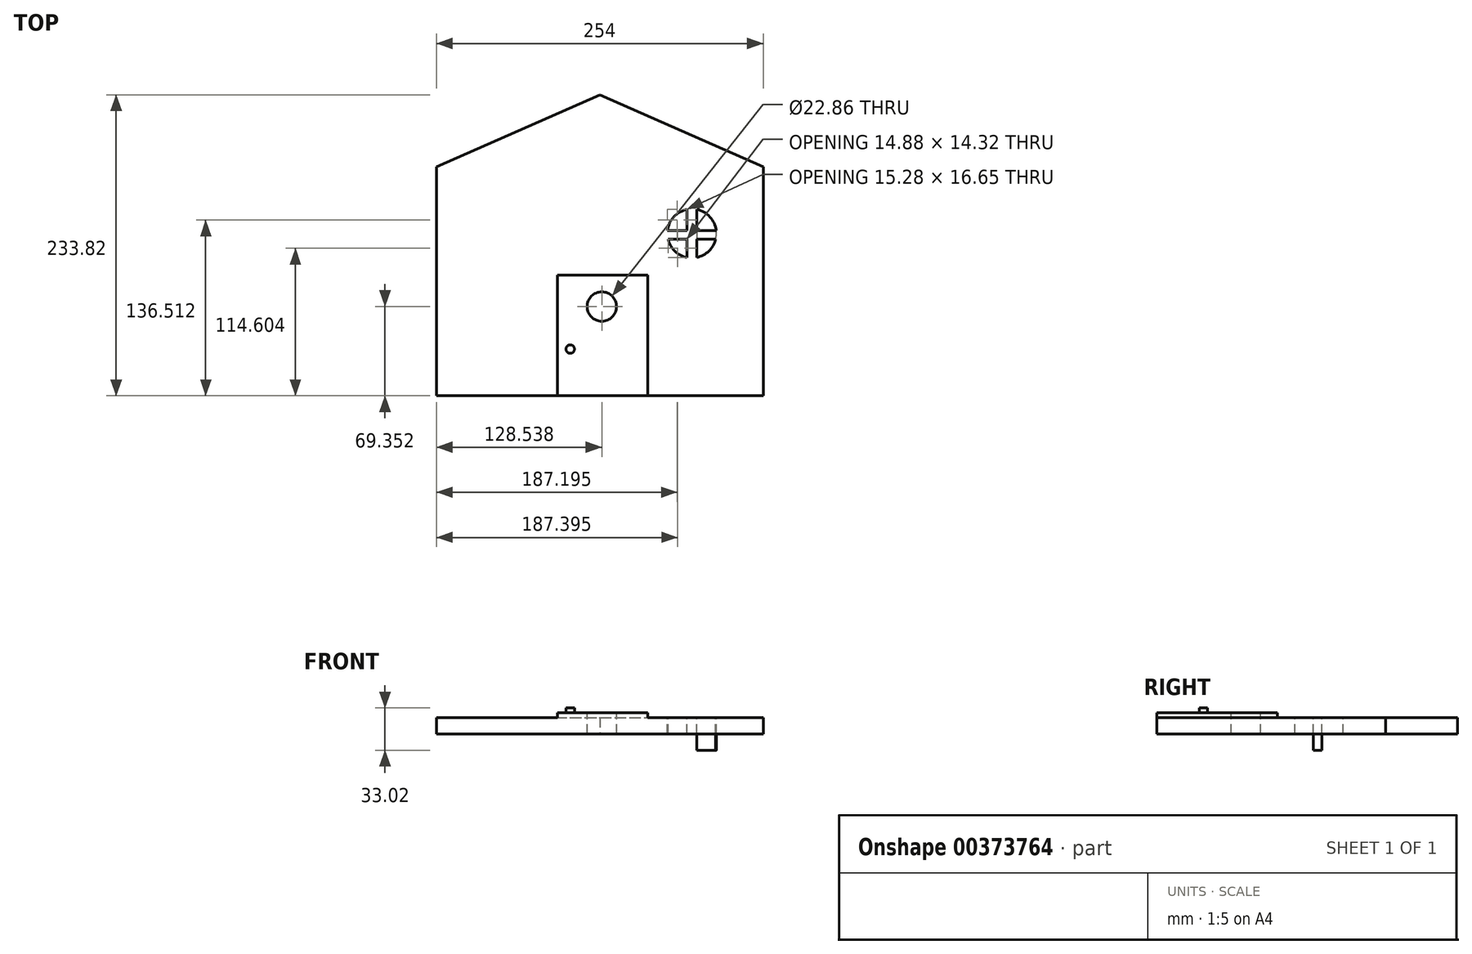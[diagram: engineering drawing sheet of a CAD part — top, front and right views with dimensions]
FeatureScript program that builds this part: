
annotation { "Feature Type Name" : "Feature", "Feature Type Description" : "" }
export const myFeature = defineFeature(function(context is Context, id is Id, definition is map)
    precondition{}
    {
        {
            var Q0;
            Q0=qCreatedBy(makeId("Top.planeOp"),FACE);
            var sketch = newSketch(context, id + "F0", { "sketchPlane" : qUnion([Q0])});
            skLineSegment(sketch, "E0.bottom", {"start": v(-400.1, 213.34) * mm, "end": v(-146.1, 213.34) * mm});
            skLineSegment(sketch, "E0.top", {"start": v(-400.1, 35.54) * mm, "end": v(-146.1, 35.54) * mm});
            skLineSegment(sketch, "E0.left", {"start": v(-400.1, 213.34) * mm, "end": v(-400.1, 35.54) * mm});
            skLineSegment(sketch, "E0.right", {"start": v(-146.1, 213.34) * mm, "end": v(-146.1, 35.54) * mm});
            skLineSegment(sketch, "E1", {"start": v(-400.1, 213.34) * mm, "end": v(-273.1, 269.36) * mm});
            skLineSegment(sketch, "E2", {"start": v(-273.1, 269.36) * mm, "end": v(-146.1, 213.34) * mm});
            skPoint(sketch, "E3", {"position": v(-273.1, 213.34) * mm});
            skSolve(sketch);
        }
        {
            var Q0;
            Q0=makeQuery(id+"F0.imprint","IMPRINT",FACE,{"disambiguationData":[TD([[makeQuery(id+"F0.imprint","IMPRINT",EDGE,{"derivedFrom":sQuery(id+"F0.wireOp",EDGE,"E0.bottom")}),-1.0]])]});
            var Q1;
            Q1=makeQuery(id+"F0.imprint","IMPRINT",FACE,{"disambiguationData":[TD([[makeQuery(id+"F0.imprint","IMPRINT",EDGE,{"derivedFrom":sQuery(id+"F0.wireOp",EDGE,"E0.bottom")}),1.0]])]});
            extrude(context, id + "F1", {"entities" : qUnion([Q0, Q1]), "depth" : 12.7 * mm});
        }
        {
            var Q0;
            Q0=makeQuery(id+"F1.opExtrude","CAP_FACE",FACE,{"disambiguationData":[OSD([sQuery(id+"F0.wireOp",EDGE,"E0.top"),sQuery(id+"F0.wireOp",EDGE,"E0.left"),sQuery(id+"F0.wireOp",EDGE,"E0.right"),sQuery(id+"F0.wireOp",EDGE,"E1"),sQuery(id+"F0.wireOp",EDGE,"E2")])],"isStart":false});
            var sketch = newSketch(context, id + "F2", { "sketchPlane" : qUnion([Q0])});
            skCircle(sketch, "E4", {"center": v(-201.6, 161.68) * mm, "radius": 18.7 * mm});
            skSolve(sketch);
        }
        {
            var Q0;
            Q0=sQuery(id+"F2.wireOp",VERTEX,"E4.center");
            var Q1;
            Q1=makeQuery(id+"F1.opExtrude","SWEPT_BODY",BODY,{"disambiguationData":[OSD([sQuery(id+"F0.wireOp",EDGE,"E0.top"),sQuery(id+"F0.wireOp",EDGE,"E0.left"),sQuery(id+"F0.wireOp",EDGE,"E0.right"),sQuery(id+"F0.wireOp",EDGE,"E1"),sQuery(id+"F0.wireOp",EDGE,"E2")])]});
            hole(context, id + "F3", {"style" : HoleStyle.SIMPLE, "endStyle" : HoleEndStyle.THROUGH, "holeDiameter" : 38.1 * mm, "isTappedThrough" : true, "tappedDepth" : 12.7 * mm, "tapClearance" : 3, "locations" : qUnion([Q0]), "scope" : qUnion([Q1])});
        }
        {
            var Q0;
            Q0=makeQuery(id+"F1.opExtrude","CAP_FACE",FACE,{"disambiguationData":[OSD([sQuery(id+"F0.wireOp",EDGE,"E0.top"),sQuery(id+"F0.wireOp",EDGE,"E0.left"),sQuery(id+"F0.wireOp",EDGE,"E0.right"),sQuery(id+"F0.wireOp",EDGE,"E1"),sQuery(id+"F0.wireOp",EDGE,"E2")])],"isStart":false});
            var sketch = newSketch(context, id + "F4", { "sketchPlane" : qUnion([Q0])});
            skLineSegment(sketch, "E5.bottom", {"start": v(-306.13, 35.54) * mm, "end": v(-236, 35.54) * mm});
            skLineSegment(sketch, "E5.top", {"start": v(-306.13, 129.3) * mm, "end": v(-236, 129.3) * mm});
            skLineSegment(sketch, "E5.left", {"start": v(-306.13, 35.54) * mm, "end": v(-306.13, 129.3) * mm});
            skLineSegment(sketch, "E5.right", {"start": v(-236, 35.54) * mm, "end": v(-236, 129.3) * mm});
            skSolve(sketch);
        }
        {
            var Q0;
            Q0=makeQuery(id+"F4.imprint","IMPRINT",FACE,{"disambiguationData":[TD([[makeQuery(id+"F4.imprint","IMPRINT",EDGE,{"derivedFrom":sQuery(id+"F4.wireOp",EDGE,"E5.bottom")}),1.0]])]});
            extrude(context, id + "F5", {"entities" : qUnion([Q0]), "operationType" : NewBodyOperationType.ADD, "depth" : 3.8 * mm});
        }
        {
            var Q0;
            Q0=makeQuery(id+"F5.opExtrude","CAP_FACE",FACE,{"disambiguationData":[OSD([sQuery(id+"F4.wireOp",EDGE,"E5.bottom"),sQuery(id+"F4.wireOp",EDGE,"E5.top"),sQuery(id+"F4.wireOp",EDGE,"E5.left"),sQuery(id+"F4.wireOp",EDGE,"E5.right")])],"isStart":false});
            var sketch = newSketch(context, id + "F6", { "sketchPlane" : qUnion([Q0])});
            skPoint(sketch, "E6", {"position": v(-271.56, 104.9) * mm});
            skSolve(sketch);
        }
        {
            var Q0;
            Q0=sQuery(id+"F6.wireOp",VERTEX,"E6");
            var Q1;
            Q1=makeQuery(id+"F1.opExtrude","SWEPT_BODY",BODY,{"disambiguationData":[OSD([sQuery(id+"F0.wireOp",EDGE,"E0.top"),sQuery(id+"F0.wireOp",EDGE,"E0.left"),sQuery(id+"F0.wireOp",EDGE,"E0.right"),sQuery(id+"F0.wireOp",EDGE,"E1"),sQuery(id+"F0.wireOp",EDGE,"E2")])]});
            hole(context, id + "F7", {"style" : HoleStyle.SIMPLE, "endStyle" : HoleEndStyle.THROUGH, "holeDiameter" : 22.86 * mm, "isTappedThrough" : true, "tappedDepth" : 12.7 * mm, "tapClearance" : 3, "locations" : qUnion([Q0]), "scope" : qUnion([Q1])});
        }
        {
            var Q0;
            Q0=makeQuery(id+"F1.opExtrude","CAP_FACE",FACE,{"disambiguationData":[OSD([sQuery(id+"F0.wireOp",EDGE,"E0.top"),sQuery(id+"F0.wireOp",EDGE,"E0.left"),sQuery(id+"F0.wireOp",EDGE,"E0.right"),sQuery(id+"F0.wireOp",EDGE,"E1"),sQuery(id+"F0.wireOp",EDGE,"E2")])],"isStart":false});
            var sketch = newSketch(context, id + "F8", { "sketchPlane" : qUnion([Q0])});
            skLineSegment(sketch, "E7", {"start": v(-205.26, 180.37) * mm, "end": v(-205.26, 142.98) * mm});
            skLineSegment(sketch, "E8", {"start": v(-197.77, 180.34) * mm, "end": v(-197.77, 143.02) * mm});
            skLineSegment(sketch, "E9", {"start": v(-220.55, 163.73) * mm, "end": v(-182.67, 163.73) * mm});
            skLineSegment(sketch, "E10", {"start": v(-183.07, 157.3) * mm, "end": v(-220.15, 157.3) * mm});
            skSolve(sketch);
        }
        {
            var Q0;
            {var subQ0=sQuery(id+"F8.wireOp",EDGE,"E7");var subQ3=sQuery(id+"F8.wireOp",EDGE,"E9");var subQ4=makeQuery(id+"F8.imprint","INTERSECT",VERTEX,{"derivedFrom":[subQ0,subQ3]});Q0=makeQuery(id+"F8.imprint","IMPRINT",FACE,{"disambiguationData":[TD([[makeQuery(id+"F8.imprint","IMPRINT",EDGE,{"disambiguationData":[TD([[subQ4,-1.0]])],"derivedFrom":subQ3}),1.0]])]});}
            extrude(context, id + "F9", {"entities" : qUnion([Q0]), "oppositeDirection" : true, "depth" : 12.7 * mm});
        }
        {
            var Q0;
            {var subQ0=sQuery(id+"F8.wireOp",EDGE,"E9");var subQ1=sQuery(id+"F8.wireOp",EDGE,"E7");var subQ2=makeQuery(id+"F8.imprint","INTERSECT",VERTEX,{"derivedFrom":[subQ1,subQ0]});Q0=makeQuery(id+"F8.imprint","IMPRINT",FACE,{"disambiguationData":[TD([[makeQuery(id+"F8.imprint","IMPRINT",EDGE,{"disambiguationData":[TD([[subQ2,-1.0]])],"derivedFrom":subQ1}),1.0]])]});}
            extrude(context, id + "F10", {"entities" : qUnion([Q0]), "operationType" : NewBodyOperationType.ADD, "oppositeDirection" : true, "depth" : 12.7 * mm});
        }
        {
            var Q0;
            {var subQ0=sQuery(id+"F8.wireOp",EDGE,"E7");var subQ3=sQuery(id+"F8.wireOp",EDGE,"E10");var subQ4=makeQuery(id+"F8.imprint","INTERSECT",VERTEX,{"derivedFrom":[subQ0,subQ3]});Q0=makeQuery(id+"F8.imprint","IMPRINT",FACE,{"disambiguationData":[TD([[makeQuery(id+"F8.imprint","IMPRINT",EDGE,{"disambiguationData":[TD([[subQ4,1.0]])],"derivedFrom":subQ3}),1.0]])]});}
            extrude(context, id + "F11", {"entities" : qUnion([Q0]), "operationType" : NewBodyOperationType.ADD, "oppositeDirection" : true, "depth" : 12.7 * mm});
        }
        {
            var Q0;
            {var subQ0=sQuery(id+"F8.wireOp",EDGE,"E9");var subQ1=sQuery(id+"F8.wireOp",EDGE,"E8");var subQ2=makeQuery(id+"F8.imprint","INTERSECT",VERTEX,{"derivedFrom":[subQ1,subQ0]});Q0=makeQuery(id+"F8.imprint","IMPRINT",FACE,{"disambiguationData":[TD([[makeQuery(id+"F8.imprint","IMPRINT",EDGE,{"disambiguationData":[TD([[subQ2,-1.0]])],"derivedFrom":subQ1}),1.0]])]});}
            extrude(context, id + "F12", {"entities" : qUnion([Q0]), "operationType" : NewBodyOperationType.ADD, "oppositeDirection" : true, "depth" : 25.4 * mm});
        }
        {
            var Q0;
            {var subQ0=sQuery(id+"F8.wireOp",EDGE,"E9");var subQ1=sQuery(id+"F8.wireOp",EDGE,"E7");var subQ2=makeQuery(id+"F8.imprint","INTERSECT",VERTEX,{"derivedFrom":[subQ1,subQ0]});Q0=makeQuery(id+"F8.imprint","IMPRINT",FACE,{"disambiguationData":[TD([[makeQuery(id+"F8.imprint","IMPRINT",EDGE,{"disambiguationData":[TD([[subQ2,-1.0]])],"derivedFrom":subQ1}),-1.0]])]});}
            extrude(context, id + "F13", {"entities" : qUnion([Q0]), "operationType" : NewBodyOperationType.ADD, "oppositeDirection" : true, "depth" : 12.7 * mm});
        }
        {
            var Q0;
            Q0=makeQuery(id+"F5.opExtrude","CAP_FACE",FACE,{"disambiguationData":[OSD([sQuery(id+"F4.wireOp",EDGE,"E5.bottom"),sQuery(id+"F4.wireOp",EDGE,"E5.top"),sQuery(id+"F4.wireOp",EDGE,"E5.left"),sQuery(id+"F4.wireOp",EDGE,"E5.right")])],"isStart":false});
            var sketch = newSketch(context, id + "F14", { "sketchPlane" : qUnion([Q0])});
            skCircle(sketch, "E11", {"center": v(-296.11, 71.8) * mm, "radius": 3.3 * mm});
            skSolve(sketch);
        }
        {
            var Q0;
            Q0=makeQuery(id+"F14.imprint","IMPRINT",FACE,{"disambiguationData":[TD([[makeQuery(id+"F14.imprint","IMPRINT",EDGE,{"derivedFrom":sQuery(id+"F14.wireOp",EDGE,"E11")}),1.0]])]});
            extrude(context, id + "F15", {"entities" : qUnion([Q0]), "operationType" : NewBodyOperationType.ADD, "depth" : 3.8 * mm});
        }
    });
